# Revit family: Pojemnik_na_papier_toaletowy POP M
name_source: partatom
category: Furniture
units: mm (PartAtom-declared; Revit-internal decimal feet)

## family parameters
Always vertical = Yes
Cut with Voids When Loaded = No
Host = Wall
Room Calculation Point = No
Shared = No

## types (1)
- Type 1
    Color / Kolor = White / Biały
    Depth / Glebokosc = 130 mm  [stored 0.426509 ft]
    Description = Pojemnik na papier toaletowy POP M to wytworzony z białego plastiku ABS naścienny dozownik, polecany do ogólnodostępnych toalet w szkołach, biurach czy gabinetach lekarskich. Posiada on atest PZH, który jest gwarancją jakości oraz potwierdzeniem wysokiego poziomu higieny. Dozownik papieru toaletowego POP M jest bardzo prosty w utrzymaniu czystości, a dzięki przeźroczystemu okienku, umożliwiającemu wygodne kontrolowanie aktualnego stanu papieru w środku, również niezwykle funkcjonalny. Jest to podajnik do rolek maxi Jumbo o średnicy do 29 cm. Dzięki uniwersalnemu wyglądowi i atrakcyjnej cenie dozownik POP M jest bardzo popularnym modelem.
    Height / Wysokosc = 325 mm  [stored 1.06627 ft]
    Manufacturer = FANECO.com
    Manufacturer code / Kod producenta = 5901764290261
    Material finish / Wykonczenie = Plastic ABS
    Model = POP M
    Product code / Kod produktu = J29PGWG
    Type Comments = Pojemnik na papier toaletowy POP M
    URL = https://faneco.com
    Weight / Waga = 0.7 kg
    Width / Szerokosc = 310 mm  [stored 1.01706 ft]

note: [stored X ft] marks values corroborated as IEEE doubles in the binary element streams (Revit-internal decimal feet)

## geometry (parser evidence)
native form markers: Blend x4, Sweep x13
no freeform markers — native parametric forms only
